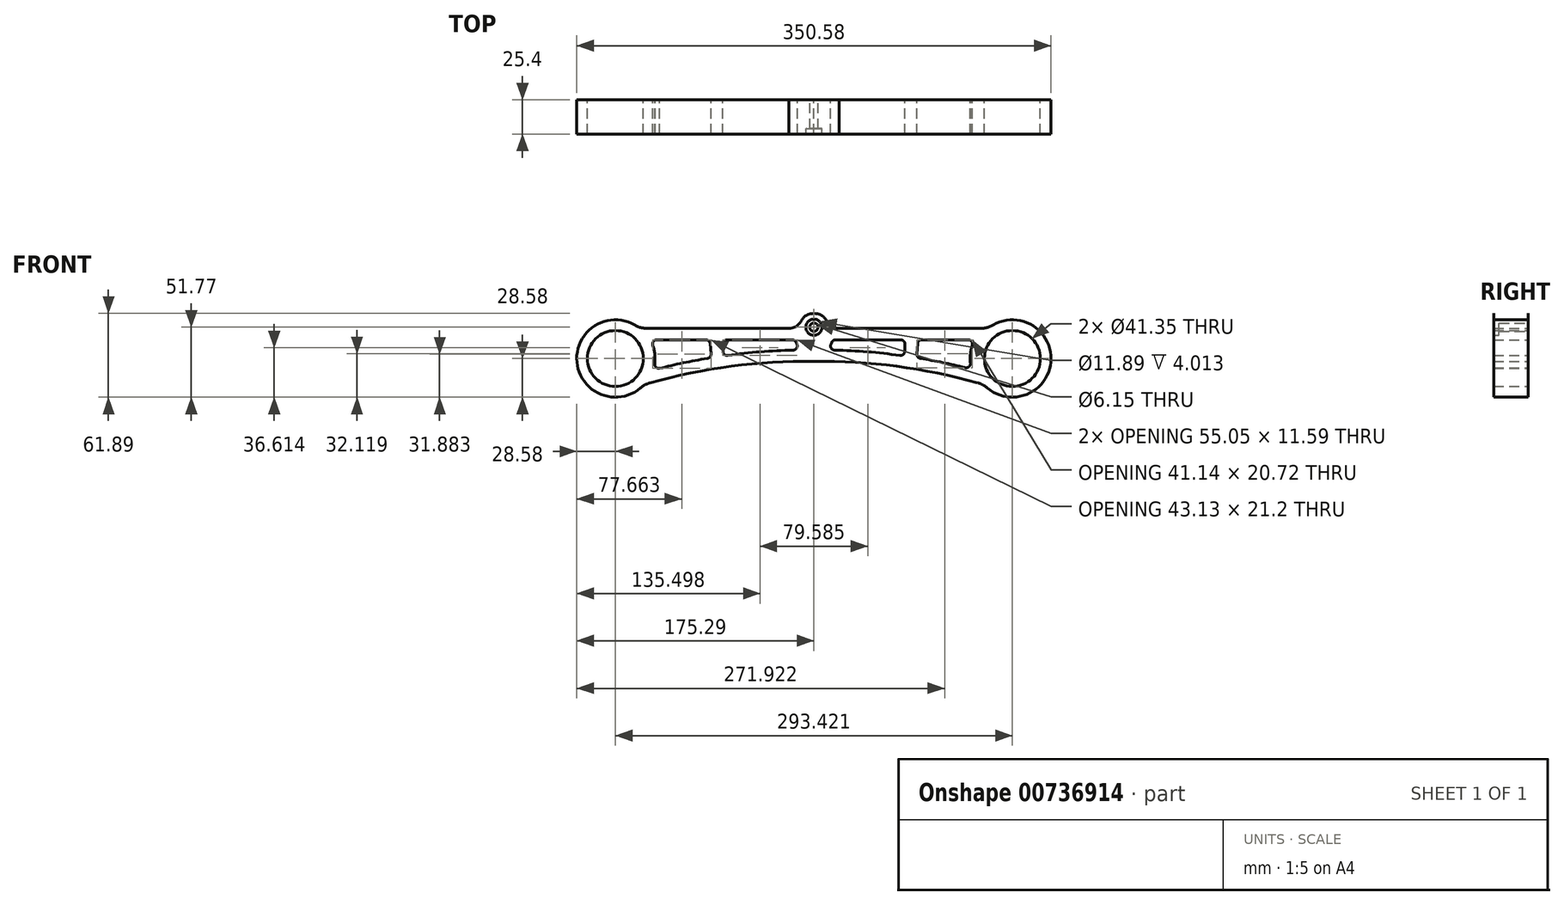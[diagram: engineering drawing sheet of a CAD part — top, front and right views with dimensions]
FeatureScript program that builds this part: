
annotation { "Feature Type Name" : "Feature", "Feature Type Description" : "" }
export const myFeature = defineFeature(function(context is Context, id is Id, definition is map)
    precondition{}
    {
        {
            var Q0;
            Q0=qCreatedBy(makeId("Front.planeOp"),FACE);
            var sketch = newSketch(context, id + "F0", { "sketchPlane" : qUnion([Q0])});
            skCircle(sketch, "E0", {"center": v(0, 0) * mm, "radius": 20.68 * mm});
            skCircle(sketch, "E1", {"center": v(293.42, 0) * mm, "radius": 20.68 * mm});
            skCircle(sketch, "E2", {"center": v(146.71, 23.2) * mm, "radius": 3.07 * mm});
            skLineSegment(sketch, "E3", {"start": v(165.26, 22.3) * mm, "end": v(269.79, 22.3) * mm});
            skArc(sketch, "E4", {"start": v(279.24, 24.8) * mm, "mid": v(321.87, -2.63) * mm, "end": v(274.94, -21.8) * mm});
            skFitSpline(sketch, "E5", {"points": [v(146.79, 33.3) * mm, v(165.26, 22.3) * mm], "startDerivative": vector(34.5, 0) * mm, "endDerivative": vector(33.63, -0.52) * mm});
            skArc(sketch, "E6", {"start": v(267.76, -17.98) * mm, "mid": v(207.8, -5.74) * mm, "end": v(146.71, -2.2) * mm});
            skCircle(sketch, "E7", {"center": v(146.71, 23.2) * mm, "radius": 5.94 * mm});
            skPoint(sketch, "E8.visualSharp", {"position": v(275.55, 22.3) * mm});
            skArc(sketch, "E8.filletArc", {"start": v(269.79, 22.3) * mm, "mid": v(274.68, 22.94) * mm, "end": v(279.24, 24.8) * mm});
            skPoint(sketch, "E9.visualSharp", {"position": v(272.34, -19.3) * mm});
            skArc(sketch, "E9.filletArc", {"start": v(274.94, -21.8) * mm, "mid": v(271.55, -19.5) * mm, "end": v(267.76, -17.98) * mm});
            skArc(sketch, "E10", {"start": v(263.77, 9.74) * mm, "mid": v(262.38, 3.29) * mm, "end": v(262.38, -3.31) * mm});
            skLineSegment(sketch, "E11", {"start": v(260.75, 13.9) * mm, "end": v(226.55, 13.87) * mm});
            skArc(sketch, "E12.filletArc", {"start": v(263.77, 9.74) * mm, "mid": v(263.32, 12.59) * mm, "end": v(260.75, 13.9) * mm});
            skArc(sketch, "E13.filletArc", {"start": v(258.42, -6.72) * mm, "mid": v(261.3, -6.06) * mm, "end": v(262.38, -3.31) * mm});
            skFitSpline(sketch, "E14.MirrorCS", {"points": [v(146.79, 33.3) * mm, v(128.16, 22.3) * mm], "startDerivative": vector(-34.5, 0) * mm, "endDerivative": vector(-33.63, -0.52) * mm});
            skLineSegment(sketch, "E15.MirrorCS", {"start": v(128.16, 22.3) * mm, "end": v(23.63, 22.3) * mm});
            skArc(sketch, "E16.MirrorCS", {"start": v(14.18, 24.8) * mm, "mid": v(-28.45, -2.63) * mm, "end": v(18.48, -21.8) * mm});
            skArc(sketch, "E17.MirrorCS", {"start": v(18.48, -21.8) * mm, "mid": v(21.87, -19.5) * mm, "end": v(25.66, -17.98) * mm});
            skArc(sketch, "E18.MirrorCS", {"start": v(23.63, 22.3) * mm, "mid": v(18.74, 22.94) * mm, "end": v(14.18, 24.8) * mm});
            skArc(sketch, "E19.MirrorCS", {"start": v(25.66, -17.98) * mm, "mid": v(85.62, -5.74) * mm, "end": v(146.71, -2.2) * mm});
            skArc(sketch, "E20", {"start": v(210.24, 2.27) * mm, "mid": v(186.23, 5) * mm, "end": v(162.09, 6.22) * mm});
            skLineSegment(sketch, "E21", {"start": v(214.03, 10.56) * mm, "end": v(213.87, 5.32) * mm});
            skLineSegment(sketch, "E22", {"start": v(210.85, 13.83) * mm, "end": v(162.73, 13.83) * mm});
            skLineSegment(sketch, "E23", {"start": v(159.85, 11.98) * mm, "end": v(159.26, 10.72) * mm});
            skPoint(sketch, "E24.visualSharp", {"position": v(157.21, 6.28) * mm});
            skArc(sketch, "E24.filletArc", {"start": v(159.26, 10.72) * mm, "mid": v(159.46, 7.7) * mm, "end": v(162.09, 6.22) * mm});
            skPoint(sketch, "E25.visualSharp", {"position": v(160.7, 13.83) * mm});
            skArc(sketch, "E25.filletArc", {"start": v(162.73, 13.83) * mm, "mid": v(161.02, 13.33) * mm, "end": v(159.85, 11.98) * mm});
            skPoint(sketch, "E26.visualSharp", {"position": v(214.12, 13.83) * mm});
            skArc(sketch, "E26.filletArc", {"start": v(214.03, 10.56) * mm, "mid": v(213.13, 12.86) * mm, "end": v(210.85, 13.83) * mm});
            skPoint(sketch, "E27.visualSharp", {"position": v(213.77, 1.73) * mm});
            skArc(sketch, "E27.filletArc", {"start": v(210.24, 2.27) * mm, "mid": v(212.74, 2.98) * mm, "end": v(213.87, 5.32) * mm});
            skArc(sketch, "E28.MirrorCS", {"start": v(130.7, 13.83) * mm, "mid": v(132.4, 13.33) * mm, "end": v(133.58, 11.98) * mm});
            skLineSegment(sketch, "E29.MirrorCS", {"start": v(133.58, 11.98) * mm, "end": v(134.16, 10.72) * mm});
            skArc(sketch, "E30.MirrorCS", {"start": v(134.16, 10.72) * mm, "mid": v(133.96, 7.7) * mm, "end": v(131.33, 6.22) * mm});
            skArc(sketch, "E31.MirrorCS", {"start": v(83.18, 2.27) * mm, "mid": v(107.2, 5) * mm, "end": v(131.33, 6.22) * mm});
            skArc(sketch, "E32.MirrorCS", {"start": v(83.18, 2.27) * mm, "mid": v(80.68, 2.98) * mm, "end": v(79.55, 5.32) * mm});
            skLineSegment(sketch, "E33.MirrorCS", {"start": v(79.4, 10.56) * mm, "end": v(79.55, 5.32) * mm});
            skArc(sketch, "E34.MirrorCS", {"start": v(79.4, 10.56) * mm, "mid": v(80.29, 12.86) * mm, "end": v(82.57, 13.83) * mm});
            skLineSegment(sketch, "E35.MirrorCS", {"start": v(82.57, 13.83) * mm, "end": v(130.7, 13.83) * mm});
            skArc(sketch, "E36", {"start": v(258.42, -6.72) * mm, "mid": v(242, -2.96) * mm, "end": v(225.44, 0.06) * mm});
            skLineSegment(sketch, "E37", {"start": v(223.39, 10.96) * mm, "end": v(222.77, 3.45) * mm});
            skPoint(sketch, "E38.visualSharp", {"position": v(223.62, 13.87) * mm});
            skArc(sketch, "E38.filletArc", {"start": v(226.55, 13.87) * mm, "mid": v(224.4, 13.03) * mm, "end": v(223.39, 10.96) * mm});
            skPoint(sketch, "E39.visualSharp", {"position": v(222.53, 0.51) * mm});
            skArc(sketch, "E39.filletArc", {"start": v(222.77, 3.45) * mm, "mid": v(223.44, 1.24) * mm, "end": v(225.44, 0.06) * mm});
            skLineSegment(sketch, "E40.MirrorCS", {"start": v(70.03, 10.96) * mm, "end": v(70.65, 3.45) * mm});
            skLineSegment(sketch, "E41.MirrorCS", {"start": v(30.68, 13.9) * mm, "end": v(66.87, 13.87) * mm});
            skArc(sketch, "E42.MirrorCS", {"start": v(27.68, 9.68) * mm, "mid": v(29.16, 3.05) * mm, "end": v(29.09, -3.73) * mm});
            skArc(sketch, "E43.MirrorCS", {"start": v(32.56, -7.3) * mm, "mid": v(29.96, -6.36) * mm, "end": v(29.09, -3.73) * mm});
            skArc(sketch, "E44.MirrorCS", {"start": v(32.56, -7.3) * mm, "mid": v(50.19, -3.2) * mm, "end": v(67.98, 0.06) * mm});
            skArc(sketch, "E45.MirrorCS", {"start": v(70.65, 3.45) * mm, "mid": v(69.98, 1.24) * mm, "end": v(67.98, 0.06) * mm});
            skArc(sketch, "E46.MirrorCS", {"start": v(66.87, 13.87) * mm, "mid": v(69.02, 13.03) * mm, "end": v(70.03, 10.96) * mm});
            skArc(sketch, "E47.MirrorCS", {"start": v(27.68, 9.68) * mm, "mid": v(28.09, 12.57) * mm, "end": v(30.68, 13.9) * mm});
            skSolve(sketch);
        }
        {
            var Q0;
            Q0=makeQuery(id+"F0.imprint","IMPRINT",FACE,{"disambiguationData":[TD([[makeQuery(id+"F0.imprint","IMPRINT",EDGE,{"derivedFrom":sQuery(id+"F0.wireOp",EDGE,"E0")}),-1.0]])]});
            extrude(context, id + "F1", {"entities" : qUnion([Q0]), "depth" : 25.4 * mm, "offsetDistance" : 25.4 * mm});
        }
        {
            var Q0;
            Q0=makeQuery(id+"F0.imprint","IMPRINT",FACE,{"disambiguationData":[TD([[makeQuery(id+"F0.imprint","IMPRINT",EDGE,{"derivedFrom":sQuery(id+"F0.wireOp",EDGE,"E2")}),-1.0]])]});
            extrude(context, id + "F2", {"entities" : qUnion([Q0]), "operationType" : NewBodyOperationType.ADD, "depth" : 21.4 * mm, "offsetDistance" : 25.4 * mm});
        }
    });
